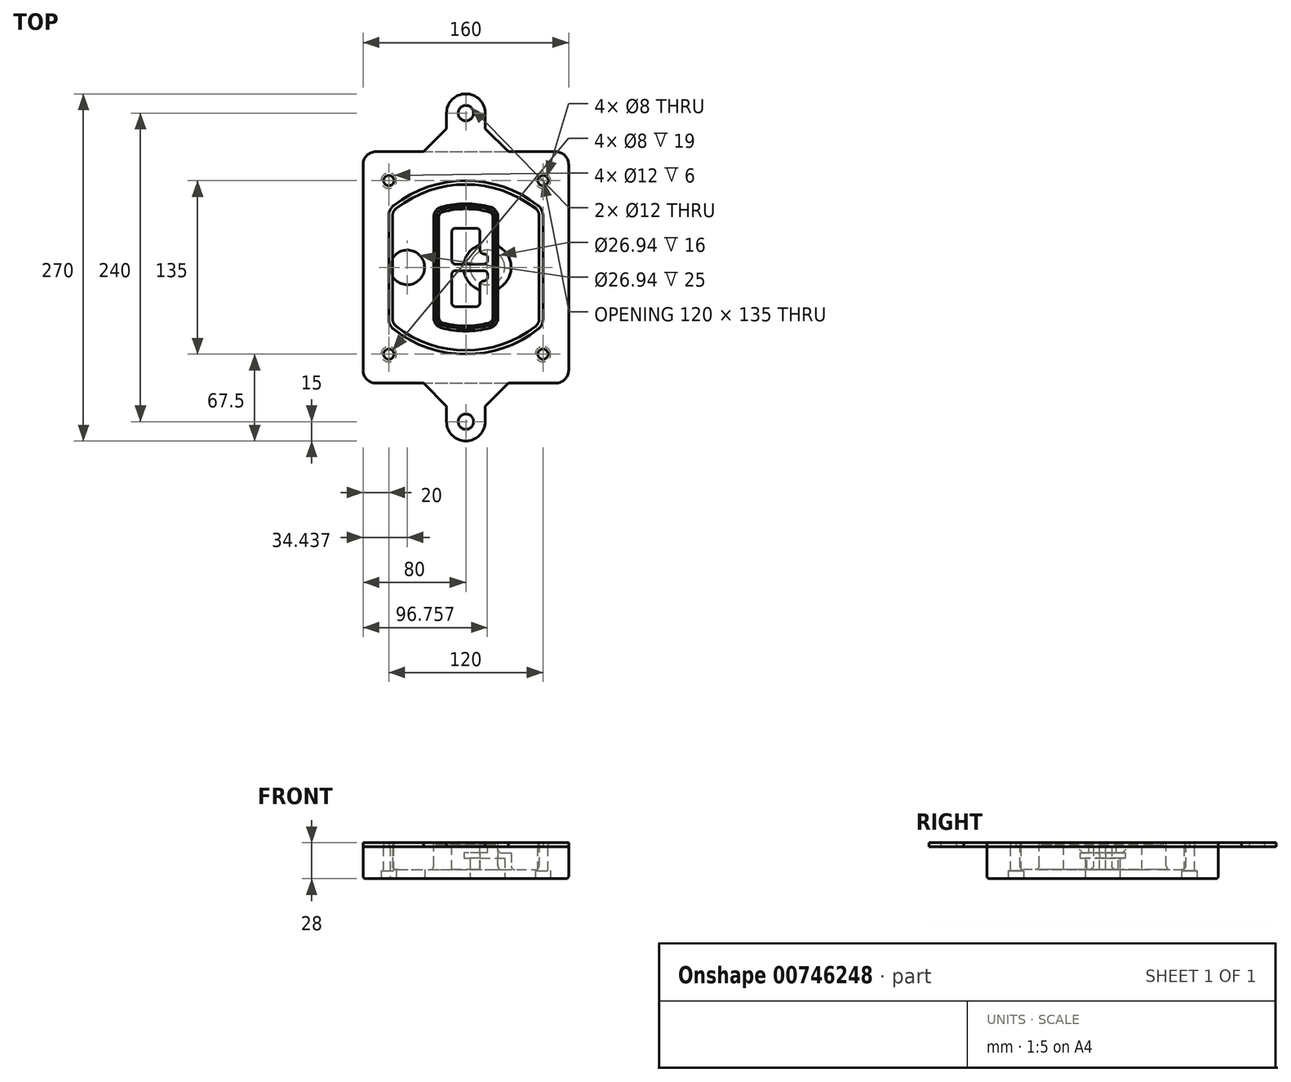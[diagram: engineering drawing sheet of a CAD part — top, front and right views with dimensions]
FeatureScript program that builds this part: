
annotation { "Feature Type Name" : "Feature", "Feature Type Description" : "" }
export const myFeature = defineFeature(function(context is Context, id is Id, definition is map)
    precondition{}
    {
        {
            var Q0;
            Q0=qCreatedBy(makeId("Top.planeOp"),FACE);
            var sketch = newSketch(context, id + "F0", { "sketchPlane" : qUnion([Q0])});
            skPoint(sketch, "E0.rect.middle", {"position": v(0, 0) * mm});
            skLineSegment(sketch, "E1.bottom", {"start": v(-70, -90) * mm, "end": v(70, -90) * mm});
            skLineSegment(sketch, "E1.top", {"start": v(-70, 90) * mm, "end": v(70, 90) * mm});
            skLineSegment(sketch, "E1.left", {"start": v(-80, -80) * mm, "end": v(-80, 80) * mm});
            skLineSegment(sketch, "E1.right", {"start": v(80, -80) * mm, "end": v(80, 80) * mm});
            skLineSegment(sketch, "E2", {"start": v(-80, 90) * mm, "end": v(80, -90) * mm, "construction": true});
            skLineSegment(sketch, "E3", {"start": v(80, 90) * mm, "end": v(-80, -90) * mm, "construction": true});
            skCircle(sketch, "E4", {"center": v(-60, 67.5) * mm, "radius": 4 * mm});
            skCircle(sketch, "E5", {"center": v(60, 67.5) * mm, "radius": 4 * mm});
            skCircle(sketch, "E6", {"center": v(60, -67.5) * mm, "radius": 4 * mm});
            skCircle(sketch, "E7", {"center": v(-60, -67.5) * mm, "radius": 4 * mm});
            skLineSegment(sketch, "E8", {"start": v(-60, 67.5) * mm, "end": v(60, 67.5) * mm, "construction": true});
            skLineSegment(sketch, "E9", {"start": v(60, 67.5) * mm, "end": v(60, -67.5) * mm, "construction": true});
            skLineSegment(sketch, "E10", {"start": v(60, -67.5) * mm, "end": v(-60, -67.5) * mm, "construction": true});
            skLineSegment(sketch, "E11", {"start": v(-60, -67.5) * mm, "end": v(-60, 67.5) * mm, "construction": true});
            skLineSegment(sketch, "E12", {"start": v(-60, 40.3) * mm, "end": v(-60, -40.3) * mm});
            skLineSegment(sketch, "E13", {"start": v(60, 40.3) * mm, "end": v(60, -40.3) * mm});
            skArc(sketch, "E14", {"start": v(56.15, 48.18) * mm, "mid": v(0, 67.5) * mm, "end": v(-56.15, 48.18) * mm});
            skArc(sketch, "E15", {"start": v(-56.15, -48.18) * mm, "mid": v(0, -67.5) * mm, "end": v(56.15, -48.18) * mm});
            skLineSegment(sketch, "E16", {"start": v(-60, 0) * mm, "end": v(60, 0) * mm, "construction": true});
            skPoint(sketch, "E17.visualSharp", {"position": v(-60, -45) * mm});
            skArc(sketch, "E17.filletArc", {"start": v(-60, -40.3) * mm, "mid": v(-58.99, -44.68) * mm, "end": v(-56.15, -48.18) * mm});
            skPoint(sketch, "E18.visualSharp", {"position": v(-60, 45) * mm});
            skArc(sketch, "E18.filletArc", {"start": v(-56.15, 48.18) * mm, "mid": v(-58.99, 44.68) * mm, "end": v(-60, 40.3) * mm});
            skPoint(sketch, "E19.visualSharp", {"position": v(60, 45) * mm});
            skArc(sketch, "E19.filletArc", {"start": v(60, 40.3) * mm, "mid": v(58.99, 44.68) * mm, "end": v(56.15, 48.18) * mm});
            skPoint(sketch, "E20.visualSharp", {"position": v(60, -45) * mm});
            skArc(sketch, "E20.filletArc", {"start": v(56.15, -48.18) * mm, "mid": v(58.99, -44.68) * mm, "end": v(60, -40.3) * mm});
            skPoint(sketch, "E21.visualSharp", {"position": v(-80, 90) * mm});
            skArc(sketch, "E21.filletArc", {"start": v(-70, 90) * mm, "mid": v(-77.07, 87.07) * mm, "end": v(-80, 80) * mm});
            skPoint(sketch, "E22.visualSharp", {"position": v(80, 90) * mm});
            skArc(sketch, "E22.filletArc", {"start": v(80, 80) * mm, "mid": v(77.07, 87.07) * mm, "end": v(70, 90) * mm});
            skPoint(sketch, "E23.visualSharp", {"position": v(80, -90) * mm});
            skArc(sketch, "E23.filletArc", {"start": v(70, -90) * mm, "mid": v(77.07, -87.07) * mm, "end": v(80, -80) * mm});
            skPoint(sketch, "E24.visualSharp", {"position": v(-80, -90) * mm});
            skArc(sketch, "E24.filletArc", {"start": v(-80, -80) * mm, "mid": v(-77.07, -87.07) * mm, "end": v(-70, -90) * mm});
            skArc(sketch, "E25.0", {"start": v(57, 40.3) * mm, "mid": v(56.3, 43.36) * mm, "end": v(54.3, 45.81) * mm});
            skLineSegment(sketch, "E25.1", {"start": v(57, 40.3) * mm, "end": v(57, -40.3) * mm});
            skArc(sketch, "E25.2", {"start": v(54.3, -45.81) * mm, "mid": v(56.3, -43.36) * mm, "end": v(57, -40.3) * mm});
            skArc(sketch, "E25.3", {"start": v(-54.3, -45.81) * mm, "mid": v(0, -64.5) * mm, "end": v(54.3, -45.81) * mm});
            skArc(sketch, "E25.4", {"start": v(-57, -40.3) * mm, "mid": v(-56.3, -43.36) * mm, "end": v(-54.3, -45.81) * mm});
            skArc(sketch, "E25.5", {"start": v(54.3, 45.81) * mm, "mid": v(0, 64.5) * mm, "end": v(-54.3, 45.81) * mm});
            skLineSegment(sketch, "E25.6", {"start": v(-57, 40.3) * mm, "end": v(-57, -40.3) * mm});
            skArc(sketch, "E25.7", {"start": v(-54.3, 45.81) * mm, "mid": v(-56.3, 43.36) * mm, "end": v(-57, 40.3) * mm});
            skArc(sketch, "E26.0", {"start": v(-58.62, 51.33) * mm, "mid": v(-62.58, 46.43) * mm, "end": v(-64, 40.3) * mm});
            skArc(sketch, "E26.1", {"start": v(58.62, 51.33) * mm, "mid": v(0, 71.5) * mm, "end": v(-58.62, 51.33) * mm});
            skArc(sketch, "E26.2", {"start": v(64, 40.3) * mm, "mid": v(62.58, 46.43) * mm, "end": v(58.62, 51.33) * mm});
            skLineSegment(sketch, "E26.3", {"start": v(64, 40.3) * mm, "end": v(64, -40.3) * mm});
            skArc(sketch, "E26.4", {"start": v(58.62, -51.33) * mm, "mid": v(62.58, -46.43) * mm, "end": v(64, -40.3) * mm});
            skLineSegment(sketch, "E26.5", {"start": v(-64, 40.3) * mm, "end": v(-64, -40.3) * mm});
            skArc(sketch, "E26.6", {"start": v(-58.62, -51.33) * mm, "mid": v(0, -71.5) * mm, "end": v(58.62, -51.33) * mm});
            skArc(sketch, "E26.7", {"start": v(-64, -40.3) * mm, "mid": v(-62.58, -46.43) * mm, "end": v(-58.62, -51.33) * mm});
            skSolve(sketch);
        }
        {
            var Q0;
            Q0=makeQuery(id+"F0.imprint","IMPRINT",FACE,{"disambiguationData":[TD([[makeQuery(id+"F0.imprint","IMPRINT",EDGE,{"derivedFrom":sQuery(id+"F0.wireOp",EDGE,"E1.bottom")}),1.0]])]});
            var Q1;
            Q1=makeQuery(id+"F0.imprint","IMPRINT",FACE,{"disambiguationData":[TD([[makeQuery(id+"F0.imprint","IMPRINT",EDGE,{"derivedFrom":sQuery(id+"F0.wireOp",EDGE,"E12")}),1.0]])]});
            var Q2;
            Q2=makeQuery(id+"F0.imprint","IMPRINT",FACE,{"disambiguationData":[TD([[makeQuery(id+"F0.imprint","IMPRINT",EDGE,{"derivedFrom":sQuery(id+"F0.wireOp",EDGE,"E25.0")}),1.0]])]});
            var Q3;
            Q3=makeQuery(id+"F0.imprint","IMPRINT",FACE,{"disambiguationData":[TD([[makeQuery(id+"F0.imprint","IMPRINT",EDGE,{"derivedFrom":sQuery(id+"F0.wireOp",EDGE,"E12")}),-1.0]])]});
            extrude(context, id + "F1", {"entities" : qUnion([Q0, Q1, Q2, Q3]), "oppositeDirection" : true, "depth" : 25 * mm});
        }
        {
            var Q0;
            Q0=makeQuery(id+"F0.imprint","IMPRINT",FACE,{"disambiguationData":[TD([[makeQuery(id+"F0.imprint","IMPRINT",EDGE,{"derivedFrom":sQuery(id+"F0.wireOp",EDGE,"E12")}),1.0]])]});
            extrude(context, id + "F2", {"entities" : qUnion([Q0]), "operationType" : NewBodyOperationType.ADD, "depth" : 3 * mm});
        }
        {
            var Q0;
            Q0=makeQuery(id+"F0.imprint","IMPRINT",FACE,{"disambiguationData":[TD([[makeQuery(id+"F0.imprint","IMPRINT",EDGE,{"derivedFrom":sQuery(id+"F0.wireOp",EDGE,"E25.0")}),1.0]])]});
            extrude(context, id + "F3", {"entities" : qUnion([Q0]), "operationType" : NewBodyOperationType.REMOVE, "oppositeDirection" : true, "depth" : 18 * mm});
        }
        {
            var Q0;
            Q0=makeQuery(id+"F2.opExtrude","CAP_FACE",FACE,{"disambiguationData":[OSD([sQuery(id+"F0.wireOp",EDGE,"E12"),sQuery(id+"F0.wireOp",EDGE,"E13"),sQuery(id+"F0.wireOp",EDGE,"E14"),sQuery(id+"F0.wireOp",EDGE,"E15"),sQuery(id+"F0.wireOp",EDGE,"E17.filletArc"),sQuery(id+"F0.wireOp",EDGE,"E18.filletArc"),sQuery(id+"F0.wireOp",EDGE,"E19.filletArc"),sQuery(id+"F0.wireOp",EDGE,"E20.filletArc"),sQuery(id+"F0.wireOp",EDGE,"E25.0"),sQuery(id+"F0.wireOp",EDGE,"E25.1"),sQuery(id+"F0.wireOp",EDGE,"E25.2"),sQuery(id+"F0.wireOp",EDGE,"E25.3"),sQuery(id+"F0.wireOp",EDGE,"E25.4"),sQuery(id+"F0.wireOp",EDGE,"E25.5"),sQuery(id+"F0.wireOp",EDGE,"E25.6"),sQuery(id+"F0.wireOp",EDGE,"E25.7")])],"isStart":false});
            var sketch = newSketch(context, id + "F4", { "sketchPlane" : qUnion([Q0])});
            skArc(sketch, "E27.0", {"start": v(-19.08, -46.97) * mm, "mid": v(0, -49.5) * mm, "end": v(19.08, -46.97) * mm});
            skArc(sketch, "E28.0", {"start": v(19.08, 46.97) * mm, "mid": v(0, 49.5) * mm, "end": v(-19.08, 46.97) * mm});
            skLineSegment(sketch, "E29", {"start": v(-25, 39.25) * mm, "end": v(-25, -39.25) * mm});
            skLineSegment(sketch, "E30", {"start": v(25, 39.25) * mm, "end": v(25, -39.25) * mm});
            skLineSegment(sketch, "E31", {"start": v(-25, 45.1) * mm, "end": v(25, 45.1) * mm, "construction": true});
            skLineSegment(sketch, "E32", {"start": v(-25, -45.1) * mm, "end": v(25, -45.1) * mm, "construction": true});
            skPoint(sketch, "E33.visualSharp", {"position": v(-25, 45.1) * mm});
            skArc(sketch, "E33.filletArc", {"start": v(-19.08, 46.97) * mm, "mid": v(-23.35, 44.11) * mm, "end": v(-25, 39.25) * mm});
            skPoint(sketch, "E34.visualSharp", {"position": v(25, 45.1) * mm});
            skArc(sketch, "E34.filletArc", {"start": v(25, 39.25) * mm, "mid": v(23.35, 44.11) * mm, "end": v(19.08, 46.97) * mm});
            skPoint(sketch, "E35.visualSharp", {"position": v(25, -45.1) * mm});
            skArc(sketch, "E35.filletArc", {"start": v(19.08, -46.97) * mm, "mid": v(23.35, -44.11) * mm, "end": v(25, -39.25) * mm});
            skPoint(sketch, "E36.visualSharp", {"position": v(-25, -45.1) * mm});
            skArc(sketch, "E36.filletArc", {"start": v(-25, -39.25) * mm, "mid": v(-23.35, -44.11) * mm, "end": v(-19.08, -46.97) * mm});
            skArc(sketch, "E37.0", {"start": v(54.3, 45.81) * mm, "mid": v(0, 64.5) * mm, "end": v(-54.3, 45.81) * mm});
            skArc(sketch, "E37.1", {"start": v(-54.3, 45.81) * mm, "mid": v(-56.3, 43.36) * mm, "end": v(-57, 40.3) * mm});
            skLineSegment(sketch, "E37.2", {"start": v(-57, 40.3) * mm, "end": v(-57, -40.3) * mm});
            skArc(sketch, "E37.3", {"start": v(-57, -40.3) * mm, "mid": v(-56.3, -43.36) * mm, "end": v(-54.3, -45.81) * mm});
            skArc(sketch, "E37.4", {"start": v(-54.3, -45.81) * mm, "mid": v(0, -64.5) * mm, "end": v(54.3, -45.81) * mm});
            skArc(sketch, "E37.5", {"start": v(54.3, -45.81) * mm, "mid": v(56.3, -43.36) * mm, "end": v(57, -40.3) * mm});
            skLineSegment(sketch, "E37.6", {"start": v(57, 40.3) * mm, "end": v(57, -40.3) * mm});
            skArc(sketch, "E37.7", {"start": v(57, 40.3) * mm, "mid": v(56.3, 43.36) * mm, "end": v(54.3, 45.81) * mm});
            skLineSegment(sketch, "E38.0", {"start": v(23, 39.25) * mm, "end": v(23, -39.25) * mm});
            skArc(sketch, "E38.1", {"start": v(18.56, -45.04) * mm, "mid": v(21.76, -42.9) * mm, "end": v(23, -39.25) * mm});
            skArc(sketch, "E38.2", {"start": v(-18.56, -45.04) * mm, "mid": v(0, -47.5) * mm, "end": v(18.56, -45.04) * mm});
            skArc(sketch, "E38.3", {"start": v(-23, -39.25) * mm, "mid": v(-21.76, -42.9) * mm, "end": v(-18.56, -45.04) * mm});
            skLineSegment(sketch, "E38.4", {"start": v(-23, 39.25) * mm, "end": v(-23, -39.25) * mm});
            skArc(sketch, "E38.5", {"start": v(23, 39.25) * mm, "mid": v(21.76, 42.9) * mm, "end": v(18.56, 45.04) * mm});
            skArc(sketch, "E38.6", {"start": v(-18.56, 45.04) * mm, "mid": v(-21.76, 42.9) * mm, "end": v(-23, 39.25) * mm});
            skArc(sketch, "E38.7", {"start": v(18.56, 45.04) * mm, "mid": v(0, 47.5) * mm, "end": v(-18.56, 45.04) * mm});
            skArc(sketch, "E39.0", {"start": v(21, 39.25) * mm, "mid": v(20.18, 41.68) * mm, "end": v(18.04, 43.1) * mm});
            skLineSegment(sketch, "E39.1", {"start": v(21, 39.25) * mm, "end": v(21, -39.25) * mm});
            skArc(sketch, "E39.2", {"start": v(18.04, -43.1) * mm, "mid": v(20.18, -41.68) * mm, "end": v(21, -39.25) * mm});
            skArc(sketch, "E39.3", {"start": v(-18.04, -43.1) * mm, "mid": v(0, -45.5) * mm, "end": v(18.04, -43.1) * mm});
            skArc(sketch, "E39.4", {"start": v(-21, -39.25) * mm, "mid": v(-20.18, -41.68) * mm, "end": v(-18.04, -43.1) * mm});
            skArc(sketch, "E39.5", {"start": v(18.04, 43.1) * mm, "mid": v(0, 45.5) * mm, "end": v(-18.04, 43.1) * mm});
            skLineSegment(sketch, "E39.6", {"start": v(-21, 39.25) * mm, "end": v(-21, -39.25) * mm});
            skArc(sketch, "E39.7", {"start": v(-18.04, 43.1) * mm, "mid": v(-20.18, 41.68) * mm, "end": v(-21, 39.25) * mm});
            skLineSegment(sketch, "E40", {"start": v(-25, 0) * mm, "end": v(25, 0) * mm, "construction": true});
            skLineSegment(sketch, "E41", {"start": v(-11, 5.5) * mm, "end": v(-11, 27.5) * mm});
            skLineSegment(sketch, "E42", {"start": v(-8, 30.5) * mm, "end": v(8, 30.5) * mm});
            skLineSegment(sketch, "E43", {"start": v(11, 27.5) * mm, "end": v(11, 13.5) * mm});
            skLineSegment(sketch, "E44", {"start": v(14, 10.5) * mm, "end": v(14, 10.5) * mm});
            skLineSegment(sketch, "E45", {"start": v(17, 7.5) * mm, "end": v(17, 5.5) * mm});
            skLineSegment(sketch, "E46", {"start": v(14, 2.5) * mm, "end": v(-8, 2.5) * mm});
            skPoint(sketch, "E47.visualSharp", {"position": v(-11, 30.5) * mm});
            skArc(sketch, "E47.filletArc", {"start": v(-8, 30.5) * mm, "mid": v(-10.12, 29.62) * mm, "end": v(-11, 27.5) * mm});
            skPoint(sketch, "E48.visualSharp", {"position": v(11, 30.5) * mm});
            skArc(sketch, "E48.filletArc", {"start": v(11, 27.5) * mm, "mid": v(10.12, 29.62) * mm, "end": v(8, 30.5) * mm});
            skPoint(sketch, "E49.visualSharp", {"position": v(11, 10.5) * mm});
            skArc(sketch, "E49.filletArc", {"start": v(11, 13.5) * mm, "mid": v(11.88, 11.38) * mm, "end": v(14, 10.5) * mm});
            skPoint(sketch, "E50.visualSharp", {"position": v(17, 10.5) * mm});
            skArc(sketch, "E50.filletArc", {"start": v(17, 7.5) * mm, "mid": v(16.12, 9.62) * mm, "end": v(14, 10.5) * mm});
            skPoint(sketch, "E51.visualSharp", {"position": v(17, 2.5) * mm});
            skArc(sketch, "E51.filletArc", {"start": v(14, 2.5) * mm, "mid": v(16.12, 3.38) * mm, "end": v(17, 5.5) * mm});
            skPoint(sketch, "E52.visualSharp", {"position": v(-11, 2.5) * mm});
            skArc(sketch, "E52.filletArc", {"start": v(-11, 5.5) * mm, "mid": v(-10.12, 3.38) * mm, "end": v(-8, 2.5) * mm});
            skLineSegment(sketch, "E53.0.MirrorCS", {"start": v(14, -2.5) * mm, "end": v(-8, -2.5) * mm});
            skArc(sketch, "E54.0.MirrorCS", {"start": v(-11, -5.5) * mm, "mid": v(-10.12, -3.38) * mm, "end": v(-8, -2.5) * mm});
            skLineSegment(sketch, "E55.0.MirrorCS", {"start": v(-11, -5.5) * mm, "end": v(-11, -27.5) * mm});
            skArc(sketch, "E56.0.MirrorCS", {"start": v(-8, -30.5) * mm, "mid": v(-10.12, -29.62) * mm, "end": v(-11, -27.5) * mm});
            skLineSegment(sketch, "E57.0.MirrorCS", {"start": v(-8, -30.5) * mm, "end": v(8, -30.5) * mm});
            skArc(sketch, "E58.0.MirrorCS", {"start": v(11, -27.5) * mm, "mid": v(10.12, -29.62) * mm, "end": v(8, -30.5) * mm});
            skLineSegment(sketch, "E59.0.MirrorCS", {"start": v(11, -27.5) * mm, "end": v(11, -13.5) * mm});
            skArc(sketch, "E60.0.MirrorCS", {"start": v(11, -13.5) * mm, "mid": v(11.88, -11.38) * mm, "end": v(14, -10.5) * mm});
            skArc(sketch, "E61.0.MirrorCS", {"start": v(17, -7.5) * mm, "mid": v(16.12, -9.62) * mm, "end": v(14, -10.5) * mm});
            skLineSegment(sketch, "E62.0.MirrorCS", {"start": v(17, -7.5) * mm, "end": v(17, -5.5) * mm});
            skArc(sketch, "E63.0.MirrorCS", {"start": v(14, -2.5) * mm, "mid": v(16.12, -3.38) * mm, "end": v(17, -5.5) * mm});
            skSolve(sketch);
        }
        {
            var Q0;
            Q0=makeQuery(id+"F4.imprint","IMPRINT",FACE,{"disambiguationData":[TD([[makeQuery(id+"F4.imprint","IMPRINT",EDGE,{"derivedFrom":sQuery(id+"F4.wireOp",EDGE,"E27.0")}),1.0]])]});
            var Q1;
            Q1=makeQuery(id+"F4.imprint","IMPRINT",FACE,{"disambiguationData":[TD([[makeQuery(id+"F4.imprint","IMPRINT",EDGE,{"derivedFrom":sQuery(id+"F4.wireOp",EDGE,"E38.0")}),-1.0]])]});
            var Q2;
            Q2=makeQuery(id+"F4.imprint","IMPRINT",FACE,{"disambiguationData":[TD([[makeQuery(id+"F4.imprint","IMPRINT",EDGE,{"derivedFrom":sQuery(id+"F4.wireOp",EDGE,"E39.0")}),1.0]])]});
            extrude(context, id + "F5", {"entities" : qUnion([Q0, Q1, Q2]), "operationType" : NewBodyOperationType.ADD, "endBound" : BoundingType.UP_TO_NEXT, "oppositeDirection" : true, "depth" : 25 * mm});
        }
        {
            var Q0;
            Q0=makeQuery(id+"F4.imprint","IMPRINT",FACE,{"disambiguationData":[TD([[makeQuery(id+"F4.imprint","IMPRINT",EDGE,{"derivedFrom":sQuery(id+"F4.wireOp",EDGE,"E38.0")}),-1.0]])]});
            extrude(context, id + "F6", {"entities" : qUnion([Q0]), "operationType" : NewBodyOperationType.REMOVE, "oppositeDirection" : true, "depth" : 2 * mm});
        }
        {
            var Q0;
            Q0=makeQuery(id+"F1.opExtrude","CAP_FACE",FACE,{"disambiguationData":[OSD([sQuery(id+"F0.wireOp",EDGE,"E1.bottom"),sQuery(id+"F0.wireOp",EDGE,"E1.top"),sQuery(id+"F0.wireOp",EDGE,"E1.left"),sQuery(id+"F0.wireOp",EDGE,"E1.right"),sQuery(id+"F0.wireOp",EDGE,"E4"),sQuery(id+"F0.wireOp",EDGE,"E5"),sQuery(id+"F0.wireOp",EDGE,"E6"),sQuery(id+"F0.wireOp",EDGE,"E7"),sQuery(id+"F0.wireOp",EDGE,"E21.filletArc"),sQuery(id+"F0.wireOp",EDGE,"E22.filletArc"),sQuery(id+"F0.wireOp",EDGE,"E23.filletArc"),sQuery(id+"F0.wireOp",EDGE,"E24.filletArc")])],"isStart":false});
            var sketch = newSketch(context, id + "F7", { "sketchPlane" : qUnion([Q0])});
            skCircle(sketch, "E64", {"center": v(16.76, 0) * mm, "radius": 13.47 * mm});
            skCircle(sketch, "E65", {"center": v(-45.56, 0) * mm, "radius": 13.47 * mm});
            skLineSegment(sketch, "E66", {"start": v(80, 0) * mm, "end": v(-80, 0) * mm});
            skCircle(sketch, "E67", {"center": v(16.76, 0) * mm, "radius": 18.47 * mm});
            skCircle(sketch, "E68", {"center": v(60, -67.5) * mm, "radius": 6 * mm});
            skCircle(sketch, "E69", {"center": v(-60, -67.5) * mm, "radius": 6 * mm});
            skCircle(sketch, "E70", {"center": v(-60, 67.5) * mm, "radius": 6 * mm});
            skCircle(sketch, "E71", {"center": v(60, 67.5) * mm, "radius": 6 * mm});
            skSolve(sketch);
        }
        {
            var Q0;
            {var subQ1=sQuery(id+"F7.wireOp",EDGE,"E66");var subQ4=sQuery(id+"F7.wireOp",EDGE,"E64");var subQ6=makeQuery(id+"F7.imprint","INTERSECT",VERTEX,{"disambiguationData":[OD(0.0)],"derivedFrom":[subQ4,subQ1]});Q0=makeQuery(id+"F7.imprint","IMPRINT",FACE,{"disambiguationData":[TD([[makeQuery(id+"F7.imprint","IMPRINT",EDGE,{"disambiguationData":[TD([[subQ6,-1.0]])],"derivedFrom":subQ4}),-1.0]])]});}
            var Q1;
            {var subQ0=sQuery(id+"F7.wireOp",EDGE,"E66");var subQ1=sQuery(id+"F7.wireOp",EDGE,"E64");var subQ3=makeQuery(id+"F7.imprint","INTERSECT",VERTEX,{"disambiguationData":[OD(0.0)],"derivedFrom":[subQ1,subQ0]});Q1=makeQuery(id+"F7.imprint","IMPRINT",FACE,{"disambiguationData":[TD([[makeQuery(id+"F7.imprint","IMPRINT",EDGE,{"disambiguationData":[TD([[subQ3,-1.0]])],"derivedFrom":subQ1}),1.0]])]});}
            var Q2;
            {var subQ0=sQuery(id+"F7.wireOp",EDGE,"E66");var subQ1=sQuery(id+"F7.wireOp",EDGE,"E64");var subQ3=makeQuery(id+"F7.imprint","INTERSECT",VERTEX,{"disambiguationData":[OD(0.0)],"derivedFrom":[subQ1,subQ0]});Q2=makeQuery(id+"F7.imprint","IMPRINT",FACE,{"disambiguationData":[TD([[makeQuery(id+"F7.imprint","IMPRINT",EDGE,{"disambiguationData":[TD([[subQ3,1.0]])],"derivedFrom":subQ1}),1.0]])]});}
            var Q3;
            {var subQ1=sQuery(id+"F7.wireOp",EDGE,"E66");var subQ4=sQuery(id+"F7.wireOp",EDGE,"E64");var subQ6=makeQuery(id+"F7.imprint","INTERSECT",VERTEX,{"disambiguationData":[OD(0.0)],"derivedFrom":[subQ4,subQ1]});Q3=makeQuery(id+"F7.imprint","IMPRINT",FACE,{"disambiguationData":[TD([[makeQuery(id+"F7.imprint","IMPRINT",EDGE,{"disambiguationData":[TD([[subQ6,1.0]])],"derivedFrom":subQ4}),-1.0]])]});}
            extrude(context, id + "F8", {"entities" : qUnion([Q0, Q1, Q2, Q3]), "operationType" : NewBodyOperationType.ADD, "oppositeDirection" : true, "depth" : 20 * mm});
        }
        {
            var Q0;
            {var subQ0=sQuery(id+"F7.wireOp",EDGE,"E66");var subQ1=sQuery(id+"F7.wireOp",EDGE,"E64");var subQ3=makeQuery(id+"F7.imprint","INTERSECT",VERTEX,{"disambiguationData":[OD(0.0)],"derivedFrom":[subQ1,subQ0]});Q0=makeQuery(id+"F7.imprint","IMPRINT",FACE,{"disambiguationData":[TD([[makeQuery(id+"F7.imprint","IMPRINT",EDGE,{"disambiguationData":[TD([[subQ3,-1.0]])],"derivedFrom":subQ1}),1.0]])]});}
            var Q1;
            {var subQ0=sQuery(id+"F7.wireOp",EDGE,"E66");var subQ1=sQuery(id+"F7.wireOp",EDGE,"E64");var subQ3=makeQuery(id+"F7.imprint","INTERSECT",VERTEX,{"disambiguationData":[OD(0.0)],"derivedFrom":[subQ1,subQ0]});Q1=makeQuery(id+"F7.imprint","IMPRINT",FACE,{"disambiguationData":[TD([[makeQuery(id+"F7.imprint","IMPRINT",EDGE,{"disambiguationData":[TD([[subQ3,1.0]])],"derivedFrom":subQ1}),1.0]])]});}
            extrude(context, id + "F9", {"entities" : qUnion([Q0, Q1]), "operationType" : NewBodyOperationType.REMOVE, "oppositeDirection" : true, "depth" : 16 * mm});
        }
        {
            var Q0;
            {var subQ0=sQuery(id+"F7.wireOp",EDGE,"E66");var subQ1=sQuery(id+"F7.wireOp",EDGE,"E65");var subQ3=makeQuery(id+"F7.imprint","INTERSECT",VERTEX,{"disambiguationData":[OD(0.0)],"derivedFrom":[subQ1,subQ0]});Q0=makeQuery(id+"F7.imprint","IMPRINT",FACE,{"disambiguationData":[TD([[makeQuery(id+"F7.imprint","IMPRINT",EDGE,{"disambiguationData":[TD([[subQ3,-1.0]])],"derivedFrom":subQ1}),1.0]])]});}
            var Q1;
            {var subQ0=sQuery(id+"F7.wireOp",EDGE,"E66");var subQ1=sQuery(id+"F7.wireOp",EDGE,"E65");var subQ3=makeQuery(id+"F7.imprint","INTERSECT",VERTEX,{"disambiguationData":[OD(0.0)],"derivedFrom":[subQ1,subQ0]});Q1=makeQuery(id+"F7.imprint","IMPRINT",FACE,{"disambiguationData":[TD([[makeQuery(id+"F7.imprint","IMPRINT",EDGE,{"disambiguationData":[TD([[subQ3,1.0]])],"derivedFrom":subQ1}),1.0]])]});}
            extrude(context, id + "F10", {"entities" : qUnion([Q0, Q1]), "operationType" : NewBodyOperationType.REMOVE, "oppositeDirection" : true, "depth" : 25 * mm});
        }
        {
            var Q0;
            Q0=makeQuery(id+"F7.imprint","IMPRINT",FACE,{"disambiguationData":[TD([[makeQuery(id+"F7.imprint","IMPRINT",EDGE,{"derivedFrom":sQuery(id+"F7.wireOp",EDGE,"E68")}),1.0]])]});
            var Q1;
            Q1=makeQuery(id+"F7.imprint","IMPRINT",FACE,{"disambiguationData":[TD([[makeQuery(id+"F7.imprint","IMPRINT",EDGE,{"derivedFrom":makeQuery(id+"F1.opExtrude","CAP_EDGE",EDGE,{"disambiguationData":[OSD([sQuery(id+"F0.wireOp",EDGE,"E5")])],"isStart":false})}),-1.0]])]});
            var Q2;
            Q2=makeQuery(id+"F7.imprint","IMPRINT",FACE,{"disambiguationData":[TD([[makeQuery(id+"F7.imprint","IMPRINT",EDGE,{"derivedFrom":sQuery(id+"F7.wireOp",EDGE,"E69")}),1.0]])]});
            var Q3;
            Q3=makeQuery(id+"F7.imprint","IMPRINT",FACE,{"disambiguationData":[TD([[makeQuery(id+"F7.imprint","IMPRINT",EDGE,{"derivedFrom":makeQuery(id+"F1.opExtrude","CAP_EDGE",EDGE,{"disambiguationData":[OSD([sQuery(id+"F0.wireOp",EDGE,"E4")])],"isStart":false})}),-1.0]])]});
            var Q4;
            Q4=makeQuery(id+"F7.imprint","IMPRINT",FACE,{"disambiguationData":[TD([[makeQuery(id+"F7.imprint","IMPRINT",EDGE,{"derivedFrom":sQuery(id+"F7.wireOp",EDGE,"E70")}),1.0]])]});
            var Q5;
            Q5=makeQuery(id+"F7.imprint","IMPRINT",FACE,{"disambiguationData":[TD([[makeQuery(id+"F7.imprint","IMPRINT",EDGE,{"derivedFrom":makeQuery(id+"F1.opExtrude","CAP_EDGE",EDGE,{"disambiguationData":[OSD([sQuery(id+"F0.wireOp",EDGE,"E7")])],"isStart":false})}),-1.0]])]});
            var Q6;
            Q6=makeQuery(id+"F7.imprint","IMPRINT",FACE,{"disambiguationData":[TD([[makeQuery(id+"F7.imprint","IMPRINT",EDGE,{"derivedFrom":sQuery(id+"F7.wireOp",EDGE,"E71")}),1.0]])]});
            var Q7;
            Q7=makeQuery(id+"F7.imprint","IMPRINT",FACE,{"disambiguationData":[TD([[makeQuery(id+"F7.imprint","IMPRINT",EDGE,{"derivedFrom":makeQuery(id+"F1.opExtrude","CAP_EDGE",EDGE,{"disambiguationData":[OSD([sQuery(id+"F0.wireOp",EDGE,"E6")])],"isStart":false})}),-1.0]])]});
            extrude(context, id + "F11", {"entities" : qUnion([Q0, Q1, Q2, Q3, Q4, Q5, Q6, Q7]), "operationType" : NewBodyOperationType.REMOVE, "oppositeDirection" : true, "depth" : 6 * mm});
        }
        {
            var Q0;
            Q0=makeQuery(id+"F9.boolean.opBoolean","COPY",FACE,{"derivedFrom":makeQuery(id+"F9.opExtrude","CAP_FACE",FACE,{"disambiguationData":[OSD([sQuery(id+"F7.wireOp",EDGE,"E64")])],"isStart":false})});
            var sketch = newSketch(context, id + "F12", { "sketchPlane" : qUnion([Q0])});
            skArc(sketch, "E72.0", {"start": v(11, 17.55) * mm, "mid": v(2.57, 11.82) * mm, "end": v(-1.54, 2.5) * mm});
            skArc(sketch, "E72.1", {"start": v(-1.54, -2.5) * mm, "mid": v(2.57, -11.82) * mm, "end": v(11, -17.55) * mm});
            skLineSegment(sketch, "E73", {"start": v(-1.54, -2.5) * mm, "end": v(14, -2.5) * mm});
            skLineSegment(sketch, "E74.0", {"start": v(14, 2.5) * mm, "end": v(-1.54, 2.5) * mm});
            skArc(sketch, "E74.1", {"start": v(14, 2.5) * mm, "mid": v(16.12, 3.38) * mm, "end": v(17, 5.5) * mm});
            skLineSegment(sketch, "E74.2", {"start": v(17, 7.5) * mm, "end": v(17, 5.5) * mm});
            skArc(sketch, "E74.3", {"start": v(17, 7.5) * mm, "mid": v(16.12, 9.62) * mm, "end": v(14, 10.5) * mm});
            skArc(sketch, "E74.4", {"start": v(11, 13.5) * mm, "mid": v(11.88, 11.38) * mm, "end": v(14, 10.5) * mm});
            skLineSegment(sketch, "E74.5", {"start": v(11, 17.55) * mm, "end": v(11, 13.5) * mm});
            skLineSegment(sketch, "E74.7", {"start": v(14, -2.5) * mm, "end": v(-1.54, -2.5) * mm});
            skArc(sketch, "E74.8", {"start": v(14, -2.5) * mm, "mid": v(16.12, -3.38) * mm, "end": v(17, -5.5) * mm});
            skLineSegment(sketch, "E74.9", {"start": v(17, -7.5) * mm, "end": v(17, -5.5) * mm});
            skArc(sketch, "E74.10", {"start": v(17, -7.5) * mm, "mid": v(16.12, -9.62) * mm, "end": v(14, -10.5) * mm});
            skArc(sketch, "E74.11", {"start": v(11, -13.5) * mm, "mid": v(11.88, -11.38) * mm, "end": v(14, -10.5) * mm});
            skLineSegment(sketch, "E74.12", {"start": v(11, -17.55) * mm, "end": v(11, -13.5) * mm});
            skPoint(sketch, "E75.orphan", {"position": v(11, -27.5) * mm});
            skPoint(sketch, "E76.orphan", {"position": v(-8, -2.5) * mm});
            skPoint(sketch, "E77.orphan", {"position": v(-8, 2.5) * mm});
            skPoint(sketch, "E78.orphan", {"position": v(11, 27.5) * mm});
            skSolve(sketch);
        }
        {
            var Q0;
            {var subQ7=sQuery(id+"F12.wireOp",EDGE,"E72.0");var subQ14=sQuery(id+"F12.wireOp",EDGE,"E72.1");var subQ16=sQuery(id+"F12.wireOp",EDGE,"E74.1");var subQ18=sQuery(id+"F12.wireOp",EDGE,"E74.8");Q0=qUnion([makeQuery(id+"F12.imprint","IMPRINT",FACE,{"disambiguationData":[TD([[makeQuery(id+"F12.imprint","IMPRINT",EDGE,{"derivedFrom":subQ7}),1.0]])]}),makeQuery(id+"F12.imprint","IMPRINT",FACE,{"disambiguationData":[TD([[makeQuery(id+"F12.imprint","IMPRINT",EDGE,{"derivedFrom":subQ14}),1.0]])]}),makeQuery(id+"F12.imprint","IMPRINT",FACE,{"disambiguationData":[TD([[makeQuery(id+"F12.imprint","IMPRINT",EDGE,{"derivedFrom":subQ16}),1.0]])]}),makeQuery(id+"F12.imprint","IMPRINT",FACE,{"disambiguationData":[TD([[makeQuery(id+"F12.imprint","IMPRINT",EDGE,{"derivedFrom":subQ18}),-1.0]])]})]);}
            var Q1;
            Q1=makeQuery(id+"F5.boolean.opBoolean","SPLIT",FACE,{"disambiguationData":[TD([makeQuery(id+"F5.opExtrude","SWEPT_FACE",FACE,{"disambiguationData":[OSD([sQuery(id+"F4.wireOp",EDGE,"E41")])]})])],"derivedFrom":makeQuery(id+"F3.boolean.opBoolean","COPY",FACE,{"derivedFrom":makeQuery(id+"F3.opExtrude","CAP_FACE",FACE,{"disambiguationData":[OSD([sQuery(id+"F0.wireOp",EDGE,"E25.0"),sQuery(id+"F0.wireOp",EDGE,"E25.1"),sQuery(id+"F0.wireOp",EDGE,"E25.2"),sQuery(id+"F0.wireOp",EDGE,"E25.3"),sQuery(id+"F0.wireOp",EDGE,"E25.4"),sQuery(id+"F0.wireOp",EDGE,"E25.5"),sQuery(id+"F0.wireOp",EDGE,"E25.6"),sQuery(id+"F0.wireOp",EDGE,"E25.7")])],"isStart":false})})});
            extrude(context, id + "F13", {"entities" : qUnion([Q0]), "operationType" : NewBodyOperationType.REMOVE, "endBound" : BoundingType.UP_TO_SURFACE, "endBoundEntityFace" : qUnion([Q1]), "depth" : 25 * mm});
        }
        {
            var Q0;
            Q0=makeQuery(id+"F3.boolean.opBoolean","COPY",EDGE,{"derivedFrom":makeQuery(id+"F3.opExtrude","CAP_EDGE",EDGE,{"disambiguationData":[OSD([sQuery(id+"F0.wireOp",EDGE,"E25.6")])],"isStart":false})});
            var Q1;
            Q1=makeQuery(id+"F8.boolean.opBoolean","INTERSECT",EDGE,{"derivedFrom":[makeQuery(id+"F5.opExtrude","SWEPT_FACE",FACE,{"disambiguationData":[OSD([sQuery(id+"F4.wireOp",EDGE,"E30")])]}),makeQuery(id+"F8.opExtrude","CAP_FACE",FACE,{"disambiguationData":[OSD([sQuery(id+"F7.wireOp",EDGE,"E67")])],"isStart":false})]});
            var Q2;
            Q2=makeQuery(id+"F8.boolean.opBoolean","INTERSECT",EDGE,{"disambiguationData":[OD(1.0)],"derivedFrom":[makeQuery(id+"F5.opExtrude","SWEPT_FACE",FACE,{"disambiguationData":[OSD([sQuery(id+"F4.wireOp",EDGE,"E30")])]}),makeQuery(id+"F8.opExtrude","SWEPT_FACE",FACE,{"disambiguationData":[OSD([sQuery(id+"F7.wireOp",EDGE,"E67")])]})]});
            var Q3;
            {var subQ0=sQuery(id+"F4.wireOp",EDGE,"E30");Q3=makeQuery(id+"F8.boolean.opBoolean","SPLIT",EDGE,{"disambiguationData":[TD([makeQuery(id+"F5.opExtrude","SWEPT_FACE",FACE,{"disambiguationData":[OSD([sQuery(id+"F4.wireOp",EDGE,"E35.filletArc")])]})])],"derivedFrom":makeQuery(id+"F5.opExtrude","CAP_EDGE",EDGE,{"disambiguationData":[OSD([subQ0])],"isStart":false})});}
            var Q4;
            {var subQ0=sQuery(id+"F0.wireOp",EDGE,"E25.7");var subQ1=sQuery(id+"F0.wireOp",EDGE,"E25.1");var subQ2=sQuery(id+"F0.wireOp",EDGE,"E25.6");var subQ3=sQuery(id+"F0.wireOp",EDGE,"E25.5");var subQ4=sQuery(id+"F0.wireOp",EDGE,"E25.4");var subQ5=sQuery(id+"F0.wireOp",EDGE,"E25.0");var subQ6=sQuery(id+"F0.wireOp",EDGE,"E25.2");var subQ7=sQuery(id+"F0.wireOp",EDGE,"E25.3");Q4=makeQuery(id+"F8.boolean.opBoolean","INTERSECT",EDGE,{"derivedFrom":[makeQuery(id+"F5.boolean.opBoolean","SPLIT",FACE,{"disambiguationData":[TD([makeQuery(id+"F2.opExtrude","SWEPT_FACE",FACE,{"disambiguationData":[OSD([subQ5])]})])],"derivedFrom":makeQuery(id+"F3.boolean.opBoolean","COPY",FACE,{"derivedFrom":makeQuery(id+"F3.opExtrude","CAP_FACE",FACE,{"disambiguationData":[OSD([subQ5,subQ1,subQ6,subQ7,subQ4,subQ3,subQ2,subQ0])],"isStart":false})})}),makeQuery(id+"F8.opExtrude","SWEPT_FACE",FACE,{"disambiguationData":[OSD([sQuery(id+"F7.wireOp",EDGE,"E67")])]})]});}
            var Q5;
            Q5=makeQuery(id+"F8.boolean.opBoolean","INTERSECT",EDGE,{"disambiguationData":[OD(0.0)],"derivedFrom":[makeQuery(id+"F5.opExtrude","SWEPT_FACE",FACE,{"disambiguationData":[OSD([sQuery(id+"F4.wireOp",EDGE,"E30")])]}),makeQuery(id+"F8.opExtrude","SWEPT_FACE",FACE,{"disambiguationData":[OSD([sQuery(id+"F7.wireOp",EDGE,"E67")])]})]});
            fillet(context, id + "F14", {"entities" : qUnion([Q0, Q1, Q2, Q3, Q4, Q5]), "radius" : 3 * mm, "tangentPropagation" : true, "allowEdgeOverflow" : false});
        }
        {
            var Q0;
            Q0=makeQuery(id+"F1.opExtrude","CAP_EDGE",EDGE,{"disambiguationData":[OSD([sQuery(id+"F0.wireOp",EDGE,"E1.bottom")])],"isStart":false});
            fillet(context, id + "F15", {"entities" : qUnion([Q0]), "radius" : 2 * mm, "tangentPropagation" : true, "allowEdgeOverflow" : false});
        }
        {
            var Q0;
            {var subQ0=sQuery(id+"F0.wireOp",EDGE,"E21.filletArc");var subQ1=sQuery(id+"F0.wireOp",EDGE,"E7");var subQ2=sQuery(id+"F0.wireOp",EDGE,"E6");var subQ3=sQuery(id+"F0.wireOp",EDGE,"E5");var subQ4=sQuery(id+"F0.wireOp",EDGE,"E4");var subQ5=sQuery(id+"F0.wireOp",EDGE,"E22.filletArc");var subQ6=sQuery(id+"F0.wireOp",EDGE,"E1.bottom");var subQ7=sQuery(id+"F0.wireOp",EDGE,"E1.right");var subQ8=sQuery(id+"F0.wireOp",EDGE,"E1.top");var subQ9=sQuery(id+"F0.wireOp",EDGE,"E1.left");var subQ10=sQuery(id+"F0.wireOp",EDGE,"E23.filletArc");var subQ11=sQuery(id+"F0.wireOp",EDGE,"E24.filletArc");Q0=makeQuery(id+"F2.boolean.opBoolean","SPLIT",FACE,{"disambiguationData":[TD([makeQuery(id+"F1.opExtrude","SWEPT_FACE",FACE,{"disambiguationData":[OSD([subQ6])]})])],"derivedFrom":makeQuery(id+"F1.opExtrude","CAP_FACE",FACE,{"disambiguationData":[OSD([subQ6,subQ8,subQ9,subQ7,subQ4,subQ3,subQ2,subQ1,subQ0,subQ5,subQ10,subQ11])],"isStart":true})});}
            var sketch = newSketch(context, id + "F16", { "sketchPlane" : qUnion([Q0])});
            skArc(sketch, "E79.0", {"start": v(56.15, 48.18) * mm, "mid": v(0, 67.5) * mm, "end": v(-56.15, 48.18) * mm});
            skArc(sketch, "E79.1", {"start": v(-56.15, 48.18) * mm, "mid": v(-58.99, 44.68) * mm, "end": v(-60, 40.3) * mm});
            skLineSegment(sketch, "E79.2", {"start": v(-60, 40.3) * mm, "end": v(-60, -40.3) * mm});
            skArc(sketch, "E79.3", {"start": v(-60, -40.3) * mm, "mid": v(-58.99, -44.68) * mm, "end": v(-56.15, -48.18) * mm});
            skArc(sketch, "E79.4", {"start": v(-56.15, -48.18) * mm, "mid": v(0, -67.5) * mm, "end": v(56.15, -48.18) * mm});
            skLineSegment(sketch, "E79.5", {"start": v(-80, -80) * mm, "end": v(-80, 80) * mm});
            skArc(sketch, "E79.6", {"start": v(-80, -80) * mm, "mid": v(-77.07, -87.07) * mm, "end": v(-70, -90) * mm});
            skCircle(sketch, "E79.7", {"center": v(-60, -67.5) * mm, "radius": 4 * mm});
            skCircle(sketch, "E79.8", {"center": v(60, -67.5) * mm, "radius": 4 * mm});
            skCircle(sketch, "E79.9", {"center": v(60, 67.5) * mm, "radius": 4 * mm});
            skLineSegment(sketch, "E79.10", {"start": v(-70, 90) * mm, "end": v(70, 90) * mm});
            skArc(sketch, "E79.11", {"start": v(-70, 90) * mm, "mid": v(-77.07, 87.07) * mm, "end": v(-80, 80) * mm});
            skCircle(sketch, "E79.12", {"center": v(-60, 67.5) * mm, "radius": 4 * mm});
            skArc(sketch, "E79.13", {"start": v(60, 40.3) * mm, "mid": v(58.99, 44.68) * mm, "end": v(56.15, 48.18) * mm});
            skLineSegment(sketch, "E79.14", {"start": v(60, 40.3) * mm, "end": v(60, -40.3) * mm});
            skArc(sketch, "E79.15", {"start": v(56.15, -48.18) * mm, "mid": v(58.99, -44.68) * mm, "end": v(60, -40.3) * mm});
            skLineSegment(sketch, "E79.16", {"start": v(-70, -90) * mm, "end": v(70, -90) * mm});
            skArc(sketch, "E79.17", {"start": v(70, -90) * mm, "mid": v(77.07, -87.07) * mm, "end": v(80, -80) * mm});
            skLineSegment(sketch, "E79.18", {"start": v(80, -80) * mm, "end": v(80, 80) * mm});
            skArc(sketch, "E79.19", {"start": v(80, 80) * mm, "mid": v(77.07, 87.07) * mm, "end": v(70, 90) * mm});
            skPoint(sketch, "E80", {"position": v(0, 90) * mm});
            skLineSegment(sketch, "E81", {"start": v(0, 90) * mm, "end": v(0, 120) * mm});
            skCircle(sketch, "E82", {"center": v(0, 120) * mm, "radius": 6 * mm});
            skPoint(sketch, "E83", {"position": v(-80, 0) * mm});
            skPoint(sketch, "E84", {"position": v(80, 0) * mm});
            skLineSegment(sketch, "E85", {"start": v(-80, 0) * mm, "end": v(80, 0) * mm, "construction": true});
            skLineSegment(sketch, "E86", {"start": v(33, 90) * mm, "end": v(15, 108) * mm});
            skLineSegment(sketch, "E87", {"start": v(15, 108) * mm, "end": v(15, 120) * mm});
            skArc(sketch, "E88", {"start": v(15, 120) * mm, "mid": v(0, 135) * mm, "end": v(-15, 120) * mm});
            skLineSegment(sketch, "E89", {"start": v(-15, 120) * mm, "end": v(-15, 108) * mm});
            skLineSegment(sketch, "E90", {"start": v(-15, 108) * mm, "end": v(-33, 90) * mm});
            skLineSegment(sketch, "E91.MirrorCS", {"start": v(15, -108) * mm, "end": v(15, -120) * mm});
            skArc(sketch, "E92.MirrorCS", {"start": v(15, -120) * mm, "mid": v(0, -135) * mm, "end": v(-15, -120) * mm});
            skLineSegment(sketch, "E93.MirrorCS", {"start": v(33, -90) * mm, "end": v(15, -108) * mm});
            skCircle(sketch, "E94.MirrorC", {"center": v(0, -120) * mm, "radius": 6 * mm});
            skLineSegment(sketch, "E95.MirrorCS", {"start": v(-15, -108) * mm, "end": v(-33, -90) * mm});
            skLineSegment(sketch, "E96.MirrorCS", {"start": v(0, -90) * mm, "end": v(0, -120) * mm});
            skLineSegment(sketch, "E97.MirrorCS", {"start": v(-15, -120) * mm, "end": v(-15, -108) * mm});
            skPoint(sketch, "E98.MirrorP", {"position": v(0, -90) * mm});
            skSolve(sketch);
        }
        {
            var Q0;
            Q0=makeQuery(id+"F16.imprint","IMPRINT",FACE,{"disambiguationData":[TD([[makeQuery(id+"F16.imprint","IMPRINT",EDGE,{"derivedFrom":sQuery(id+"F16.wireOp",EDGE,"E82")}),-1.0]])]});
            var Q1;
            Q1=makeQuery(id+"F16.imprint","IMPRINT",FACE,{"disambiguationData":[TD([[makeQuery(id+"F16.imprint","IMPRINT",EDGE,{"derivedFrom":sQuery(id+"F16.wireOp",EDGE,"E79.0")}),-1.0]])]});
            var Q2;
            Q2=makeQuery(id+"F16.imprint","IMPRINT",FACE,{"disambiguationData":[TD([[makeQuery(id+"F16.imprint","IMPRINT",EDGE,{"derivedFrom":sQuery(id+"F16.wireOp",EDGE,"E91.MirrorCS")}),-1.0]])]});
            var Q3;
            Q3=makeQuery(id+"F2.opExtrude","CAP_FACE",FACE,{"disambiguationData":[OSD([sQuery(id+"F0.wireOp",EDGE,"E12"),sQuery(id+"F0.wireOp",EDGE,"E13"),sQuery(id+"F0.wireOp",EDGE,"E14"),sQuery(id+"F0.wireOp",EDGE,"E15"),sQuery(id+"F0.wireOp",EDGE,"E17.filletArc"),sQuery(id+"F0.wireOp",EDGE,"E18.filletArc"),sQuery(id+"F0.wireOp",EDGE,"E19.filletArc"),sQuery(id+"F0.wireOp",EDGE,"E20.filletArc"),sQuery(id+"F0.wireOp",EDGE,"E25.0"),sQuery(id+"F0.wireOp",EDGE,"E25.1"),sQuery(id+"F0.wireOp",EDGE,"E25.2"),sQuery(id+"F0.wireOp",EDGE,"E25.3"),sQuery(id+"F0.wireOp",EDGE,"E25.4"),sQuery(id+"F0.wireOp",EDGE,"E25.5"),sQuery(id+"F0.wireOp",EDGE,"E25.6"),sQuery(id+"F0.wireOp",EDGE,"E25.7")])],"isStart":false});
            extrude(context, id + "F17", {"entities" : qUnion([Q0, Q1, Q2]), "endBound" : BoundingType.UP_TO_SURFACE, "depth" : 4 * mm, "endBoundEntityFace" : qUnion([Q3]), "offsetDistance" : 25 * mm});
        }
    });
